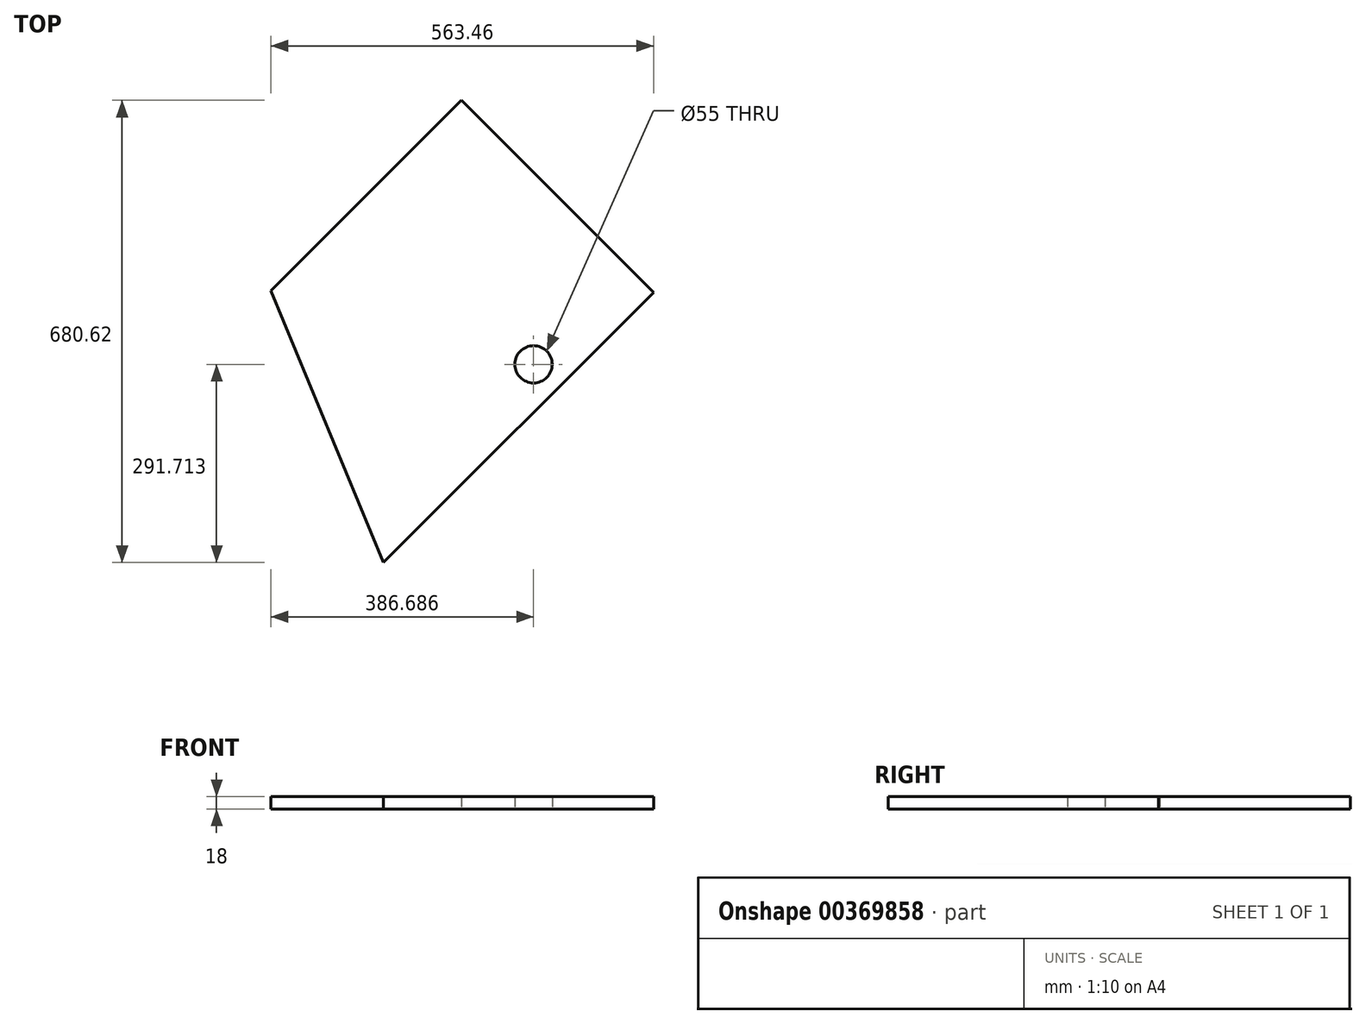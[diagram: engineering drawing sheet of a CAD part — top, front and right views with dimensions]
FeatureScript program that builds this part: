
annotation { "Feature Type Name" : "Feature", "Feature Type Description" : "" }
export const myFeature = defineFeature(function(context is Context, id is Id, definition is map)
    precondition{}
    {
        {
            var Q0;
            Q0=qCreatedBy(makeId("Top.planeOp"),FACE);
            var sketch = newSketch(context, id + "F0", { "sketchPlane" : qUnion([Q0])});
            skLineSegment(sketch, "E0", {"start": v(0, 0) * mm, "end": v(1194.54, 0) * mm, "construction": true});
            skLineSegment(sketch, "E1", {"start": v(1194.54, 0) * mm, "end": v(1592.32, 397.78) * mm});
            skLineSegment(sketch, "E2", {"start": v(400, 400) * mm, "end": v(0, 0) * mm, "construction": true});
            skLineSegment(sketch, "E3", {"start": v(1592.32, 397.78) * mm, "end": v(1309.48, 680.62) * mm});
            skLineSegment(sketch, "E4", {"start": v(1309.48, 680.62) * mm, "end": v(1028.86, 400) * mm});
            skLineSegment(sketch, "E5", {"start": v(1028.86, 400) * mm, "end": v(400, 400) * mm, "construction": true});
            skLineSegment(sketch, "E6", {"start": v(1605.05, 385.05) * mm, "end": v(1202, -18) * mm, "construction": true});
            skLineSegment(sketch, "E7", {"start": v(1202, -18) * mm, "end": v(-18, -18) * mm, "construction": true});
            skLineSegment(sketch, "E8", {"start": v(-30.73, -5.27) * mm, "end": v(374.54, 400) * mm, "construction": true});
            skLineSegment(sketch, "E9", {"start": v(-30.73, -5.27) * mm, "end": v(-18, -18) * mm, "construction": true});
            skLineSegment(sketch, "E10", {"start": v(-18, -18) * mm, "end": v(-18, -18) * mm});
            skCircle(sketch, "E11", {"center": v(1415.55, 291.71) * mm, "radius": 27.5 * mm});
            skLineSegment(sketch, "E12", {"start": v(1028.86, 400) * mm, "end": v(1194.54, 0) * mm});
            skSolve(sketch);
        }
        {
            var Q0;
            Q0=makeQuery(id+"F0.imprint","IMPRINT",FACE,{"disambiguationData":[TD([[makeQuery(id+"F0.imprint","IMPRINT",EDGE,{"derivedFrom":sQuery(id+"F0.wireOp",EDGE,"E0")}),1.0]])]});
            var Q1;
            Q1=makeQuery(id+"F0.imprint","IMPRINT",FACE,{"disambiguationData":[TD([[makeQuery(id+"F0.imprint","IMPRINT",EDGE,{"derivedFrom":sQuery(id+"F0.wireOp",EDGE,"E1")}),1.0]])]});
            extrude(context, id + "F1", {"entities" : qUnion([Q0, Q1]), "depth" : 18 * mm});
        }
    });
